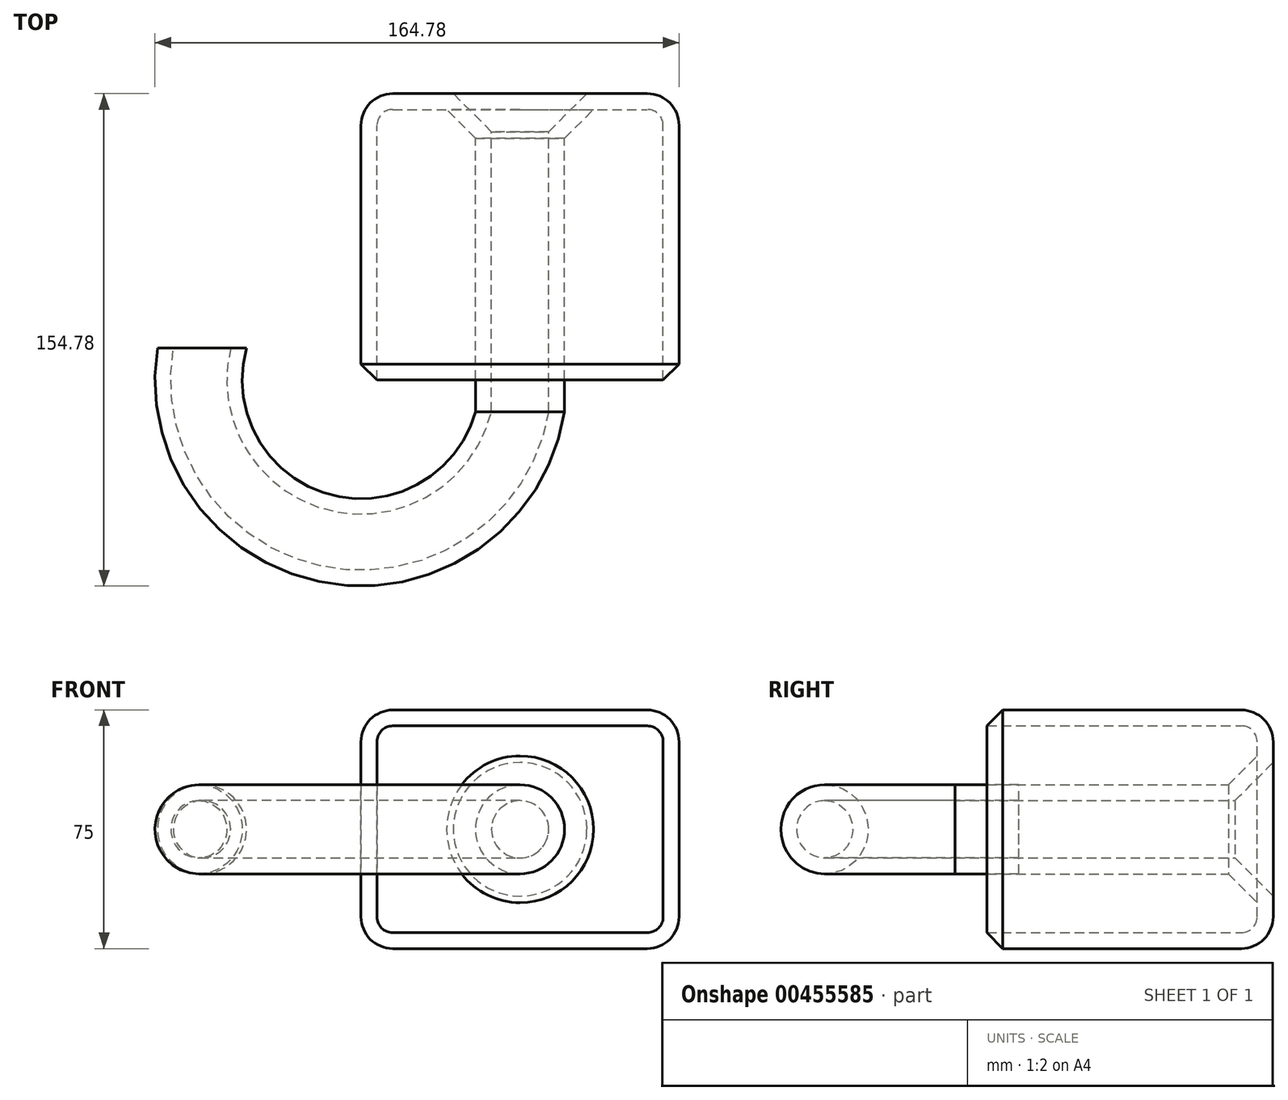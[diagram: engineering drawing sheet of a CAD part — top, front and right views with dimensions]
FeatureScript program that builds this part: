
annotation { "Feature Type Name" : "Feature", "Feature Type Description" : "" }
export const myFeature = defineFeature(function(context is Context, id is Id, definition is map)
    precondition{}
    {
        {
            var Q0;
            Q0=qCreatedBy(makeId("Front.planeOp"),FACE);
            var sketch = newSketch(context, id + "F0", { "sketchPlane" : qUnion([Q0])});
            skLineSegment(sketch, "E0.bottom", {"start": v(-50, 37.5) * mm, "end": v(50, 37.5) * mm});
            skLineSegment(sketch, "E0.top", {"start": v(-50, -37.5) * mm, "end": v(50, -37.5) * mm});
            skLineSegment(sketch, "E0.left", {"start": v(-50, 37.5) * mm, "end": v(-50, -37.5) * mm});
            skLineSegment(sketch, "E0.right", {"start": v(50, 37.5) * mm, "end": v(50, -37.5) * mm});
            skSolve(sketch);
        }
        {
            var Q0;
            Q0 = qSketchRegion(id + "F0", true);
            extrude(context, id + "F1", {"entities" : qUnion([Q0]), "depth" : 100 * mm});
        }
        {
            var Q0;
            Q0=makeQuery(id+"F1.opExtrude","SWEPT_FACE",FACE,{"disambiguationData":[OSD([sQuery(id+"F0.wireOp",EDGE,"E0.bottom")])]});
            var Q1;
            Q1=makeQuery(id+"F1.opExtrude","CAP_FACE",FACE,{"disambiguationData":[OSD([sQuery(id+"F0.wireOp",EDGE,"E0.bottom"),sQuery(id+"F0.wireOp",EDGE,"E0.top"),sQuery(id+"F0.wireOp",EDGE,"E0.left"),sQuery(id+"F0.wireOp",EDGE,"E0.right")])],"isStart":false});
            var Q2;
            Q2=makeQuery(id+"F1.opExtrude","SWEPT_FACE",FACE,{"disambiguationData":[OSD([sQuery(id+"F0.wireOp",EDGE,"E0.right")])]});
            var Q3;
            Q3=makeQuery(id+"F1.opExtrude","SWEPT_FACE",FACE,{"disambiguationData":[OSD([sQuery(id+"F0.wireOp",EDGE,"E0.top")])]});
            var Q4;
            Q4=makeQuery(id+"F1.opExtrude","CAP_FACE",FACE,{"disambiguationData":[OSD([sQuery(id+"F0.wireOp",EDGE,"E0.bottom"),sQuery(id+"F0.wireOp",EDGE,"E0.top"),sQuery(id+"F0.wireOp",EDGE,"E0.left"),sQuery(id+"F0.wireOp",EDGE,"E0.right")])],"isStart":true});
            fillet(context, id + "F2", {"entities" : qUnion([Q0, Q1, Q2, Q3, Q4]), "radius" : 10 * mm, "tangentPropagation" : true, "allowEdgeOverflow" : false});
        }
        {
            var Q0;
            Q0=qCreatedBy(makeId("Front.planeOp"),FACE);
            var sketch = newSketch(context, id + "F3", { "sketchPlane" : qUnion([Q0])});
            skPoint(sketch, "E1", {"position": v(0, 0) * mm});
            skSolve(sketch);
        }
        {
            var Q0;
            Q0=sQuery(id+"F3.wireOp",VERTEX,"E1");
            var Q1;
            Q1=makeQuery(id+"F1.opExtrude","SWEPT_BODY",BODY,{"disambiguationData":[OSD([sQuery(id+"F0.wireOp",EDGE,"E0.bottom"),sQuery(id+"F0.wireOp",EDGE,"E0.top"),sQuery(id+"F0.wireOp",EDGE,"E0.left"),sQuery(id+"F0.wireOp",EDGE,"E0.right")])]});
            hole(context, id + "F4", {"style" : HoleStyle.C_SINK, "endStyle" : HoleEndStyle.THROUGH, "oppositeDirection" : true, "standardTappedOrClearance" : lookupTablePath({ "fit" : "Normal", "standard" : "ISO", "engagement" : "75%", "pitch" : "2 mm", "size" : "M20", "type" : "Tapped" }), "standardBlindInLast" : lookupTablePath({ "fit" : "Standard", "standard" : "ISO", "engagement" : "75%", "pitch" : "2 mm", "size" : "M20", "type" : "Tapped" }), "holeDiameter" : 18 * mm, "cSinkDiameter" : 42 * mm, "cSinkAngle" : 90 * degree, "showTappedDepth" : true, "isTappedThrough" : true, "tappedDepth" : 12 * mm, "tapClearance" : 3, "locations" : qUnion([Q0]), "scope" : qUnion([Q1]), "majorDiameter" : 20 * mm});
        }
        {
            var Q0;
            {var subQ0=sQuery(id+"F0.wireOp",EDGE,"E0.bottom");Q0=makeQuery(id+"F2.opFillet","BLEND_FACE",FACE,{"disambiguationData":[OSD([subQ0]),TDD([makeQuery(id+"F1.opExtrude","CAP_EDGE",EDGE,{"disambiguationData":[OSD([subQ0])],"isStart":false})])]});}
            var Q1;
            Q1=makeQuery(id+"F1.opExtrude","CAP_FACE",FACE,{"disambiguationData":[OSD([sQuery(id+"F0.wireOp",EDGE,"E0.bottom"),sQuery(id+"F0.wireOp",EDGE,"E0.top"),sQuery(id+"F0.wireOp",EDGE,"E0.left"),sQuery(id+"F0.wireOp",EDGE,"E0.right")])],"isStart":false});
            var Q2;
            {var subQ0=sQuery(id+"F0.wireOp",EDGE,"E0.right");var subQ1=sQuery(id+"F0.wireOp",EDGE,"E0.bottom");Q2=makeQuery(id+"F2.opFillet","BLEND_FACE",FACE,{"disambiguationData":[OSD([subQ1,subQ0]),TDD([makeQuery(id+"F1.opExtrude","CAP_VERTEX",VERTEX,{"disambiguationData":[OSD([subQ1,subQ0])],"isStart":false})])]});}
            var Q3;
            {var subQ0=sQuery(id+"F0.wireOp",EDGE,"E0.right");Q3=makeQuery(id+"F2.opFillet","BLEND_FACE",FACE,{"disambiguationData":[OSD([subQ0]),TDD([makeQuery(id+"F1.opExtrude","CAP_EDGE",EDGE,{"disambiguationData":[OSD([subQ0])],"isStart":false})])]});}
            var Q4;
            {var subQ0=sQuery(id+"F0.wireOp",EDGE,"E0.top");Q4=makeQuery(id+"F2.opFillet","BLEND_FACE",FACE,{"disambiguationData":[OSD([subQ0]),TDD([makeQuery(id+"F1.opExtrude","CAP_EDGE",EDGE,{"disambiguationData":[OSD([subQ0])],"isStart":false})])]});}
            var Q5;
            {var subQ0=sQuery(id+"F0.wireOp",EDGE,"E0.right");var subQ1=sQuery(id+"F0.wireOp",EDGE,"E0.top");Q5=makeQuery(id+"F2.opFillet","BLEND_FACE",FACE,{"disambiguationData":[OSD([subQ1,subQ0]),TDD([makeQuery(id+"F1.opExtrude","CAP_VERTEX",VERTEX,{"disambiguationData":[OSD([subQ1,subQ0])],"isStart":false})])]});}
            var Q6;
            {var subQ0=sQuery(id+"F0.wireOp",EDGE,"E0.left");Q6=makeQuery(id+"F2.opFillet","BLEND_FACE",FACE,{"disambiguationData":[OSD([subQ0]),TDD([makeQuery(id+"F1.opExtrude","CAP_EDGE",EDGE,{"disambiguationData":[OSD([subQ0])],"isStart":false})])]});}
            var Q7;
            {var subQ0=sQuery(id+"F0.wireOp",EDGE,"E0.left");var subQ1=sQuery(id+"F0.wireOp",EDGE,"E0.top");Q7=makeQuery(id+"F2.opFillet","BLEND_FACE",FACE,{"disambiguationData":[OSD([subQ1,subQ0]),TDD([makeQuery(id+"F1.opExtrude","CAP_VERTEX",VERTEX,{"disambiguationData":[OSD([subQ1,subQ0])],"isStart":false})])]});}
            var Q8;
            {var subQ0=sQuery(id+"F0.wireOp",EDGE,"E0.left");var subQ1=sQuery(id+"F0.wireOp",EDGE,"E0.bottom");Q8=makeQuery(id+"F2.opFillet","BLEND_FACE",FACE,{"disambiguationData":[OSD([subQ1,subQ0]),TDD([makeQuery(id+"F1.opExtrude","CAP_VERTEX",VERTEX,{"disambiguationData":[OSD([subQ1,subQ0])],"isStart":false})])]});}
            shell(context, id + "F5", {"entities" : qUnion([Q0, Q1, Q2, Q3, Q4, Q5, Q6, Q7, Q8]), "thickness" : 5 * mm});
        }
        {
            var Q0;
            Q0=makeQuery(id+"F1.opExtrude","CAP_FACE",FACE,{"disambiguationData":[OSD([sQuery(id+"F0.wireOp",EDGE,"E0.bottom"),sQuery(id+"F0.wireOp",EDGE,"E0.top"),sQuery(id+"F0.wireOp",EDGE,"E0.left"),sQuery(id+"F0.wireOp",EDGE,"E0.right")])],"isStart":false});
            var Q1;
            {var subQ0=sQuery(id+"F0.wireOp",EDGE,"E0.left");Q1=makeQuery(id+"F2.opFillet","BLEND_EDGE",EDGE,{"blendedFrom":[makeQuery(id+"F1.opExtrude","CAP_EDGE",EDGE,{"disambiguationData":[OSD([subQ0])],"isStart":false}),makeQuery(id+"F1.opExtrude","SWEPT_FACE",FACE,{"disambiguationData":[OSD([subQ0])]})],"blendedInto":[makeQuery(id+"F1.opExtrude","SWEPT_FACE",FACE,{"disambiguationData":[OSD([subQ0])]})]});}
            revolve(context, id + "F6", {"operationType" : NewBodyOperationType.ADD, "entities" : qUnion([Q0]), "axis" : qUnion([Q1]), "revolveType" : RevolveType.ONE_DIRECTION, "angle" : 90 * degree});
        }
        {
            var Q0;
            Q0=makeQuery(id+"F6.opRevolve","CAP_FACE",FACE,{"disambiguationData":[OSD([sQuery(id+"F0.wireOp",EDGE,"E0.bottom"),sQuery(id+"F0.wireOp",EDGE,"E0.top"),sQuery(id+"F0.wireOp",EDGE,"E0.left"),sQuery(id+"F0.wireOp",EDGE,"E0.right")])],"isStart":false});
            var Q1;
            {var subQ0=sQuery(id+"F0.wireOp",EDGE,"E0.left");Q1=makeQuery(id+"F2.opFillet","BLEND_EDGE",EDGE,{"blendedFrom":[makeQuery(id+"F1.opExtrude","CAP_EDGE",EDGE,{"disambiguationData":[OSD([subQ0])],"isStart":false}),makeQuery(id+"F1.opExtrude","SWEPT_FACE",FACE,{"disambiguationData":[OSD([subQ0])]})],"blendedInto":[makeQuery(id+"F1.opExtrude","SWEPT_FACE",FACE,{"disambiguationData":[OSD([subQ0])]})]});}
            revolve(context, id + "F7", {"operationType" : NewBodyOperationType.ADD, "entities" : qUnion([Q0]), "axis" : qUnion([Q1]), "revolveType" : RevolveType.ONE_DIRECTION, "angle" : 90 * degree});
        }
        {
            var Q0;
            Q0=makeQuery(id+"F1.opExtrude","SWEPT_FACE",FACE,{"disambiguationData":[OSD([sQuery(id+"F0.wireOp",EDGE,"E0.bottom")])]});
            var Q1;
            Q1=makeQuery(id+"F1.opExtrude","SWEPT_FACE",FACE,{"disambiguationData":[OSD([sQuery(id+"F0.wireOp",EDGE,"E0.right")])]});
            var Q2;
            {var subQ0=sQuery(id+"F0.wireOp",EDGE,"E0.right");var subQ1=sQuery(id+"F0.wireOp",EDGE,"E0.bottom");Q2=makeQuery(id+"F2.opFillet","BLEND_EDGE",EDGE,{"blendedFrom":[makeQuery(id+"F1.opExtrude","CAP_VERTEX",VERTEX,{"disambiguationData":[OSD([subQ1,subQ0])],"isStart":false}),makeQuery(id+"F1.opExtrude","SWEPT_EDGE",EDGE,{"disambiguationData":[OSD([subQ1,subQ0])]})],"blendedInto":[]});}
            var Q3;
            {var subQ0=sQuery(id+"F0.wireOp",EDGE,"E0.right");var subQ1=sQuery(id+"F0.wireOp",EDGE,"E0.top");Q3=makeQuery(id+"F2.opFillet","BLEND_EDGE",EDGE,{"blendedFrom":[makeQuery(id+"F1.opExtrude","CAP_VERTEX",VERTEX,{"disambiguationData":[OSD([subQ1,subQ0])],"isStart":false}),makeQuery(id+"F1.opExtrude","SWEPT_EDGE",EDGE,{"disambiguationData":[OSD([subQ1,subQ0])]})],"blendedInto":[]});}
            chamfer(context, id + "F8", {"entities" : qUnion([Q0, Q1, Q2, Q3]), "width" : 5 * mm, "tangentPropagation" : true});
        }
    });
